# Revit family: AH66-212-BSG
name_source: partatom
category: Communication Devices
revit_build: Autodesk Revit 2014 (Build: 20140709_2115(x64)
units: mm (PartAtom-declared; Revit-internal decimal feet)

## types (1)
- Full-Range, Outdoor, Horn Loudspeaker
    100V Taps = 32.00 W
    70V Taps = 32.00 W
    Baffle Material = <By Category>
    Body Material = Default
    Color = <By Category>
    Cost = 2802.99 $
    Cost MSRP = 2802.99 $
    Coverage Horizontal = 65.00°
    Coverage Vertical = 65.00°
    Depth = 47.68 "
    Description = 3-WAY STADIUM HORN LOUDSPEAKER WITH 65° X 65° COVERAGE PATTERN
    Dispersion Angle = 65.00°
    Enclosure Material = <By Category>
    Family Code (default) = LOUD SPEAKERS
    Frequency Response  = 100Hz - 17kHz (-10 to +4dB)
    Grill Material = QF_Plastic - Black - Fine Textured
    Height = 32.53 "
    IQ Category = SPEAKERS
    Impedance = 8
    Ingress Protection = IP45 When Tilted 5° Downwards
    Input Connectors = Barrier Terminal
    Manufacturer = ATLAS SOUND
    Manufacturer URL = https://www.atlasied.com
    Market = Commercial, Higher Education, Emergency
    MasterFormat = 27 41 13
    MaterFormat Title = SPEAKERS
    Maximum Output = 128dB
    Model = AH66-212-BSG
    Mount Material = Default
    OmniClass Number = 23-37 17 13 19
    OmniClass Title = SPEAKERS
    Pitch = 0.00°
    Power Handling = 750
    Power Rating (RMS) = 750 Watts
    Product Documentation Link = https://www.atlasied.com
    Product Page URL = https://www.atlasied.com
    Rotation = 0.00°
    SPL Max = 134
    ScheduleType |RF| = AtlasIED Master
    Sensitivity = 105.5
    Speaker Dispersion = 65.00°
    Speaker Type = S1
    Transformer Option = Yes
    URL = www.atlassound.com
    Vertical Symmetry = Yes
    Warranty = 5 Year
    Weight Product = 300
    Width = 32.53 "

## geometry (parser evidence)
native form markers: Blend x4, Sweep x7
no freeform markers — native parametric forms only
